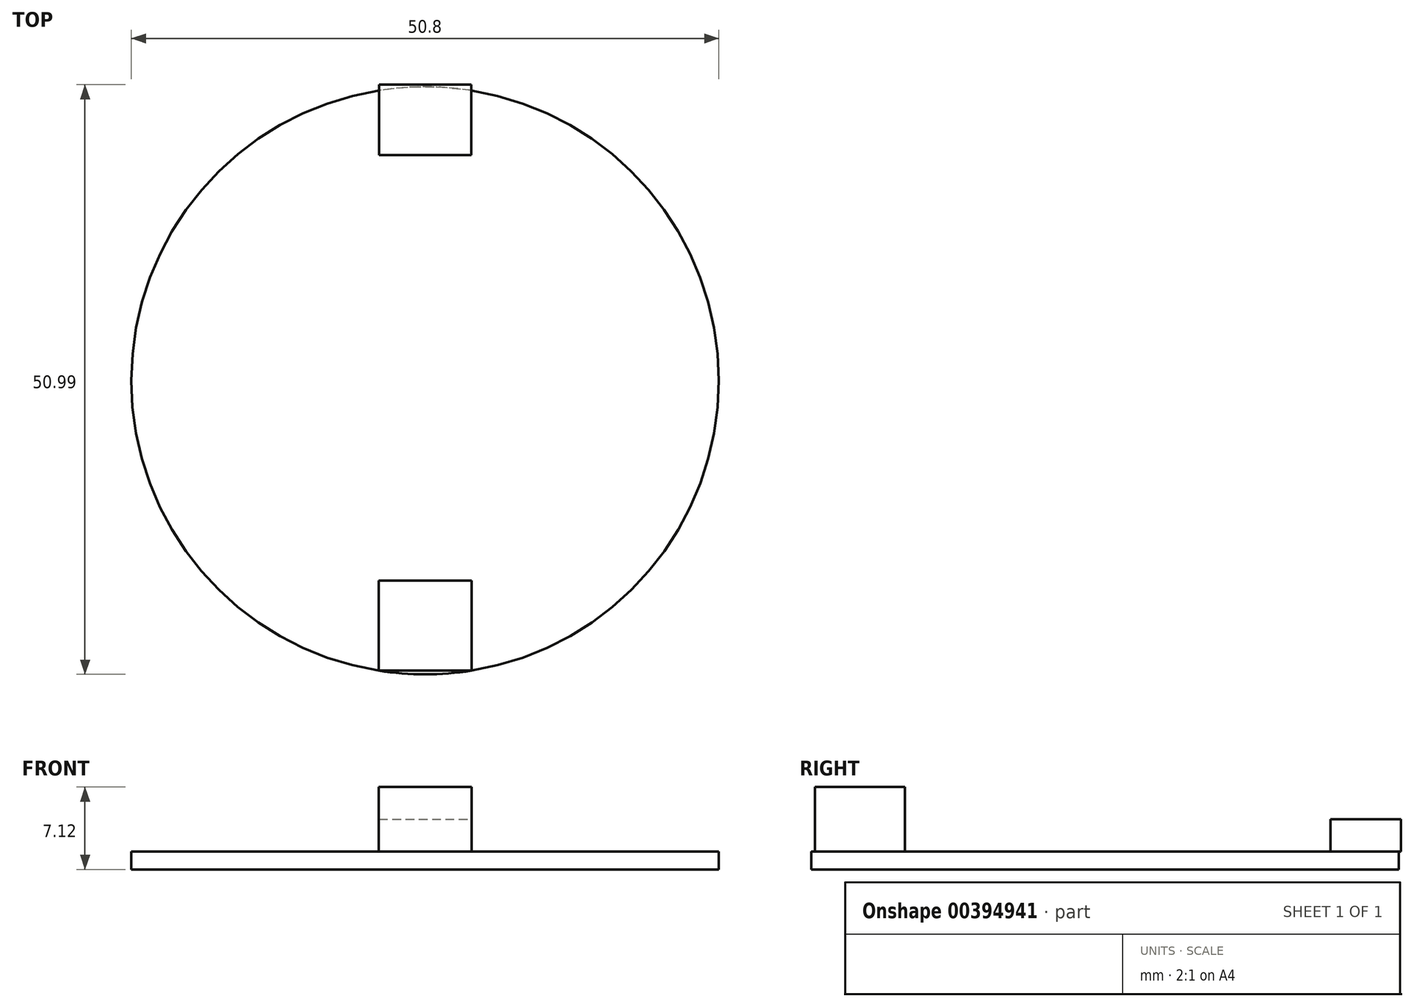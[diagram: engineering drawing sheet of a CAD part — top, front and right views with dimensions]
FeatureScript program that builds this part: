
annotation { "Feature Type Name" : "Feature", "Feature Type Description" : "" }
export const myFeature = defineFeature(function(context is Context, id is Id, definition is map)
    precondition{}
    {
        {
            var Q0;
            Q0=qCreatedBy(makeId("Top.planeOp"),FACE);
            var sketch = newSketch(context, id + "F0", { "sketchPlane" : qUnion([Q0])});
            skCircle(sketch, "E0", {"center": v(0, 0) * mm, "radius": 25.4 * mm});
            skSolve(sketch);
        }
        {
            var Q0;
            Q0 = qSketchRegion(id + "F0", true);
            extrude(context, id + "F1", {"entities" : qUnion([Q0]), "depth" : 1.54 * mm});
        }
        {
            var Q0;
            Q0=makeQuery(id+"F1.opExtrude","CAP_FACE",FACE,{"disambiguationData":[OSD([sQuery(id+"F0.wireOp",EDGE,"E0")])],"isStart":false});
            var sketch = newSketch(context, id + "F2", { "sketchPlane" : qUnion([Q0])});
            skLineSegment(sketch, "E1.bottom", {"start": v(-4.01, -25.08) * mm, "end": v(4.01, -25.08) * mm});
            skLineSegment(sketch, "E1.top", {"start": v(-4.01, -17.3) * mm, "end": v(4.01, -17.3) * mm});
            skLineSegment(sketch, "E1.left", {"start": v(-4.01, -25.08) * mm, "end": v(-4.01, -17.3) * mm});
            skLineSegment(sketch, "E1.right", {"start": v(4.01, -25.08) * mm, "end": v(4.01, -17.3) * mm});
            skSolve(sketch);
        }
        {
            var Q0;
            Q0 = qSketchRegion(id + "F2", true);
            extrude(context, id + "F3", {"entities" : qUnion([Q0]), "operationType" : NewBodyOperationType.ADD, "depth" : 5.6 * mm});
        }
        {
            var Q0;
            {var subQ0=sQuery(id+"F0.wireOp",EDGE,"E0");var subQ1=makeQuery(id+"F1.opExtrude","CAP_FACE",FACE,{"disambiguationData":[OSD([subQ0])],"isStart":false});Q0=makeQuery(id+"F3.boolean.opBoolean","SPLIT",FACE,{"disambiguationData":[TD([makeQuery(id+"F1.opExtrude","SWEPT_FACE",FACE,{"disambiguationData":[OSD([subQ0])]}),subQ1,makeQuery(id+"F3.opExtrude","SWEPT_FACE",FACE,{"disambiguationData":[OSD([sQuery(id+"F2.wireOp",EDGE,"E1.bottom")])]}),makeQuery(id+"F3.opExtrude","SWEPT_FACE",FACE,{"disambiguationData":[OSD([sQuery(id+"F2.wireOp",EDGE,"E1.top")])]}),makeQuery(id+"F3.opExtrude","SWEPT_FACE",FACE,{"disambiguationData":[OSD([sQuery(id+"F2.wireOp",EDGE,"E1.left")])]}),makeQuery(id+"F3.opExtrude","SWEPT_FACE",FACE,{"disambiguationData":[OSD([sQuery(id+"F2.wireOp",EDGE,"E1.right")])]})])],"derivedFrom":subQ1});}
            var sketch = newSketch(context, id + "F4", { "sketchPlane" : qUnion([Q0])});
            skLineSegment(sketch, "E2.bottom", {"start": v(-3.99, 25.09) * mm, "end": v(3.99, 25.09) * mm, "construction": true});
            skLineSegment(sketch, "E2.top", {"start": v(-3.99, 19.5) * mm, "end": v(3.99, 19.5) * mm});
            skLineSegment(sketch, "E2.left", {"start": v(-3.99, 25.09) * mm, "end": v(-3.99, 19.5) * mm});
            skLineSegment(sketch, "E2.right", {"start": v(3.99, 25.09) * mm, "end": v(3.99, 19.5) * mm});
            skLineSegment(sketch, "E3.top", {"start": v(-3.99, 25.6) * mm, "end": v(3.99, 25.6) * mm});
            skLineSegment(sketch, "E3.left", {"start": v(-3.99, 25.09) * mm, "end": v(-3.99, 25.6) * mm});
            skLineSegment(sketch, "E3.right", {"start": v(3.99, 25.09) * mm, "end": v(3.99, 25.6) * mm});
            skSolve(sketch);
        }
        {
            var Q0;
            Q0=makeQuery(id+"F4.imprint","IMPRINT",FACE,{"disambiguationData":[TD([[makeQuery(id+"F4.imprint","IMPRINT",EDGE,{"derivedFrom":sQuery(id+"F4.wireOp",EDGE,"E2.top")}),1.0]])]});
            var Q1;
            Q1=makeQuery(id+"F4.imprint","IMPRINT",FACE,{"disambiguationData":[TD([[makeQuery(id+"F4.imprint","IMPRINT",EDGE,{"derivedFrom":sQuery(id+"F4.wireOp",EDGE,"E3.top")}),-1.0]])]});
            extrude(context, id + "F5", {"entities" : qUnion([Q0, Q1]), "operationType" : NewBodyOperationType.ADD, "depth" : 2.8 * mm});
        }
    });
